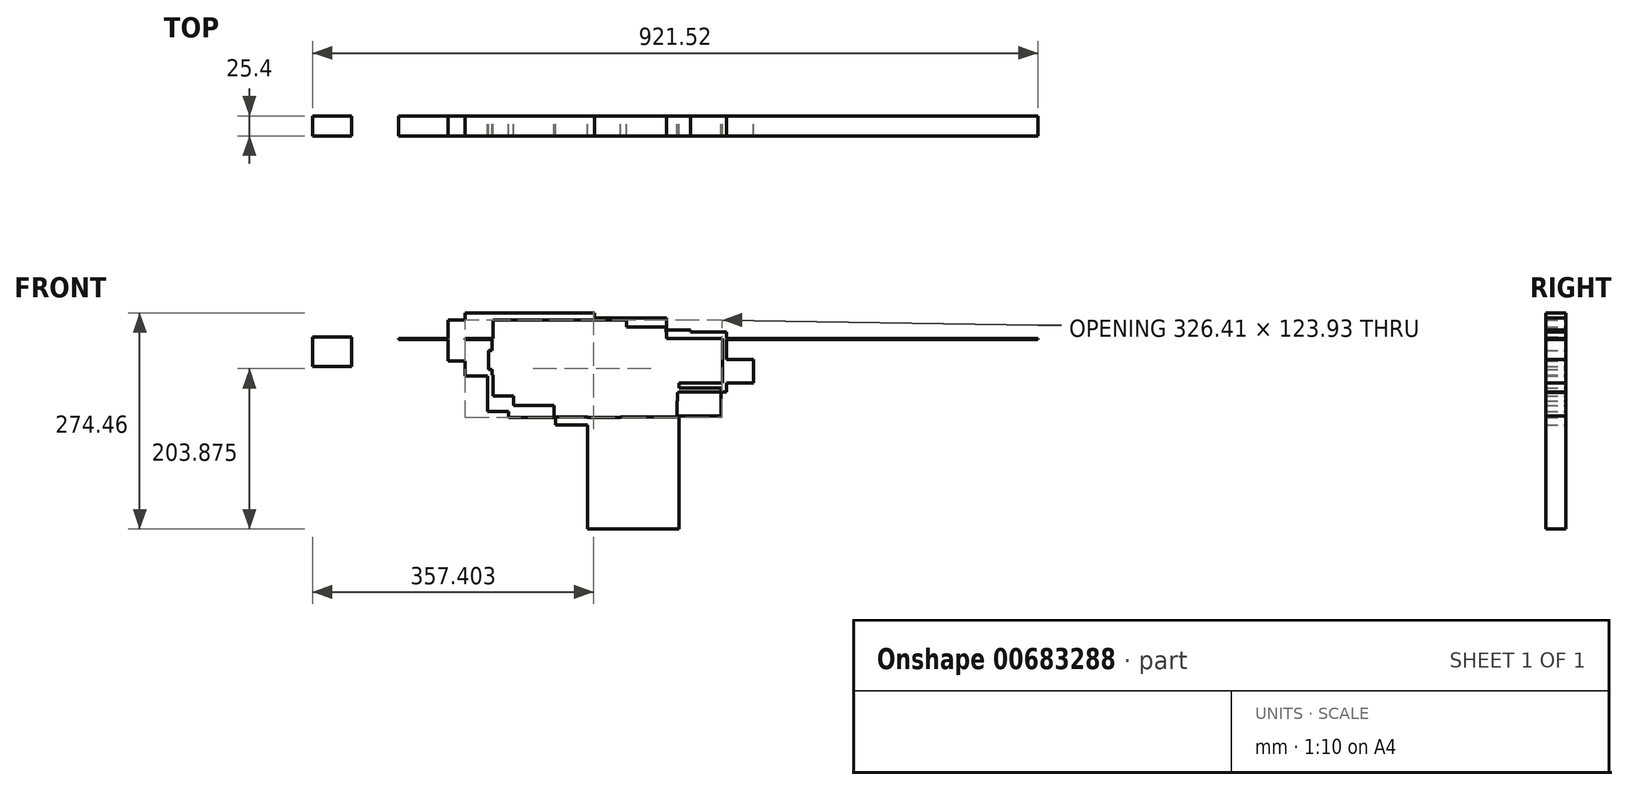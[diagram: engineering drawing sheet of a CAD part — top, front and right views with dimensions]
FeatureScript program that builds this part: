
annotation { "Feature Type Name" : "Feature", "Feature Type Description" : "" }
export const myFeature = defineFeature(function(context is Context, id is Id, definition is map)
    precondition{}
    {
        {
            var Q0;
            Q0=qCreatedBy(makeId("Front.planeOp"),FACE);
            var sketch = newSketch(context, id + "F0", { "sketchPlane" : qUnion([Q0])});
            skLineSegment(sketch, "E0.bottom", {"start": v(0, 0) * mm, "end": v(49.91, 0) * mm});
            skLineSegment(sketch, "E0.top", {"start": v(0, 37.47) * mm, "end": v(49.91, 37.47) * mm});
            skLineSegment(sketch, "E0.left", {"start": v(0, 0) * mm, "end": v(0, 37.47) * mm});
            skLineSegment(sketch, "E0.right", {"start": v(49.91, 0) * mm, "end": v(49.91, 37.47) * mm});
            skLineSegment(sketch, "E1.bottom", {"start": v(49.91, -36.2) * mm, "end": v(49.91, -36.2) * mm});
            skLineSegment(sketch, "E1.top", {"start": v(49.91, -12.83) * mm, "end": v(49.91, -12.83) * mm});
            skLineSegment(sketch, "E1.left", {"start": v(49.91, -36.2) * mm, "end": v(49.91, -12.83) * mm});
            skLineSegment(sketch, "E1.right", {"start": v(49.91, -36.2) * mm, "end": v(49.91, -12.83) * mm});
            skLineSegment(sketch, "E2.bottom", {"start": v(109.35, 35.43) * mm, "end": v(921.52, 35.43) * mm});
            skLineSegment(sketch, "E2.top", {"start": v(109.35, 34.42) * mm, "end": v(921.52, 34.42) * mm});
            skLineSegment(sketch, "E2.left", {"start": v(109.35, 35.43) * mm, "end": v(109.35, 34.42) * mm});
            skLineSegment(sketch, "E2.right", {"start": v(921.52, 35.43) * mm, "end": v(921.52, 34.42) * mm});
            skLineSegment(sketch, "E3.bottom", {"start": v(355.75, -9.52) * mm, "end": v(429.42, -9.52) * mm});
            skLineSegment(sketch, "E3.top", {"start": v(355.75, 31.07) * mm, "end": v(429.42, 31.07) * mm});
            skLineSegment(sketch, "E3.left", {"start": v(355.75, -9.52) * mm, "end": v(355.75, 31.07) * mm});
            skLineSegment(sketch, "E3.right", {"start": v(429.42, -9.52) * mm, "end": v(429.42, 31.07) * mm});
            skLineSegment(sketch, "E4.bottom", {"start": v(518.7, -27.12) * mm, "end": v(397.54, -27.12) * mm});
            skLineSegment(sketch, "E4.top", {"start": v(518.7, -63.04) * mm, "end": v(397.54, -63.04) * mm});
            skLineSegment(sketch, "E4.left", {"start": v(518.7, -27.12) * mm, "end": v(518.7, -63.04) * mm});
            skLineSegment(sketch, "E4.right", {"start": v(397.54, -27.12) * mm, "end": v(397.54, -63.04) * mm});
            skLineSegment(sketch, "E5.bottom", {"start": v(443.51, -56.93) * mm, "end": v(222.77, -56.93) * mm});
            skLineSegment(sketch, "E5.top", {"start": v(443.51, -4.85) * mm, "end": v(222.77, -4.85) * mm});
            skLineSegment(sketch, "E5.left", {"start": v(443.51, -56.93) * mm, "end": v(443.51, -4.85) * mm});
            skLineSegment(sketch, "E5.right", {"start": v(222.77, -56.93) * mm, "end": v(222.77, -4.85) * mm});
            skLineSegment(sketch, "E6.bottom", {"start": v(391.37, -64.48) * mm, "end": v(249.08, -64.48) * mm});
            skLineSegment(sketch, "E6.top", {"start": v(391.37, -7) * mm, "end": v(249.08, -7) * mm});
            skLineSegment(sketch, "E6.left", {"start": v(391.37, -64.48) * mm, "end": v(391.37, -7) * mm});
            skLineSegment(sketch, "E6.right", {"start": v(249.08, -64.48) * mm, "end": v(249.08, -7) * mm});
            skLineSegment(sketch, "E7.bottom", {"start": v(434.23, -49.4) * mm, "end": v(255.22, -49.4) * mm});
            skLineSegment(sketch, "E7.top", {"start": v(434.23, 18.86) * mm, "end": v(255.22, 18.86) * mm});
            skLineSegment(sketch, "E7.left", {"start": v(434.23, -49.4) * mm, "end": v(434.23, 18.86) * mm});
            skLineSegment(sketch, "E7.right", {"start": v(255.22, -49.4) * mm, "end": v(255.22, 18.86) * mm});
            skLineSegment(sketch, "E8.bottom", {"start": v(520.6, -32.87) * mm, "end": v(304.97, -32.87) * mm});
            skLineSegment(sketch, "E8.top", {"start": v(520.6, 44) * mm, "end": v(304.97, 44) * mm});
            skLineSegment(sketch, "E8.left", {"start": v(520.6, -32.87) * mm, "end": v(520.6, 44) * mm});
            skLineSegment(sketch, "E8.right", {"start": v(304.97, -32.87) * mm, "end": v(304.97, 44) * mm});
            skLineSegment(sketch, "E9.bottom", {"start": v(480.04, -0.9) * mm, "end": v(321.76, -0.9) * mm});
            skLineSegment(sketch, "E9.top", {"start": v(480.04, 46.16) * mm, "end": v(321.76, 46.16) * mm});
            skLineSegment(sketch, "E9.left", {"start": v(480.04, -0.9) * mm, "end": v(480.04, 46.16) * mm});
            skLineSegment(sketch, "E9.right", {"start": v(321.76, -0.9) * mm, "end": v(321.76, 46.16) * mm});
            skLineSegment(sketch, "E10.bottom", {"start": v(560.47, -20.65) * mm, "end": v(323.75, -20.65) * mm});
            skLineSegment(sketch, "E10.top", {"start": v(560.47, 8.8) * mm, "end": v(323.75, 8.8) * mm});
            skLineSegment(sketch, "E10.left", {"start": v(560.47, -20.65) * mm, "end": v(560.47, 8.8) * mm});
            skLineSegment(sketch, "E10.right", {"start": v(323.75, -20.65) * mm, "end": v(323.75, 8.8) * mm});
            skLineSegment(sketch, "E11.bottom", {"start": v(526.1, -32.5) * mm, "end": v(287.37, -32.5) * mm});
            skLineSegment(sketch, "E11.top", {"start": v(526.1, 44) * mm, "end": v(287.37, 44) * mm});
            skLineSegment(sketch, "E11.left", {"start": v(526.1, -32.5) * mm, "end": v(526.1, 44) * mm});
            skLineSegment(sketch, "E11.right", {"start": v(287.37, -32.5) * mm, "end": v(287.37, 44) * mm});
            skLineSegment(sketch, "E12.bottom", {"start": v(378.2, -5.2) * mm, "end": v(240.43, -5.2) * mm});
            skLineSegment(sketch, "E12.top", {"start": v(378.2, 32.15) * mm, "end": v(240.43, 32.15) * mm});
            skLineSegment(sketch, "E12.left", {"start": v(378.2, -5.2) * mm, "end": v(378.2, 32.15) * mm});
            skLineSegment(sketch, "E12.right", {"start": v(240.43, -5.2) * mm, "end": v(240.43, 32.15) * mm});
            skLineSegment(sketch, "E13.bottom", {"start": v(449.66, -37.18) * mm, "end": v(229.4, -37.18) * mm});
            skLineSegment(sketch, "E13.top", {"start": v(449.66, 61.96) * mm, "end": v(229.4, 61.96) * mm});
            skLineSegment(sketch, "E13.left", {"start": v(449.66, -37.18) * mm, "end": v(449.66, 61.96) * mm});
            skLineSegment(sketch, "E13.right", {"start": v(229.4, -37.18) * mm, "end": v(229.4, 61.96) * mm});
            skLineSegment(sketch, "E14.bottom", {"start": v(388.16, 3.05) * mm, "end": v(269.8, 3.05) * mm});
            skLineSegment(sketch, "E14.top", {"start": v(388.16, 28.2) * mm, "end": v(269.8, 28.2) * mm});
            skLineSegment(sketch, "E14.left", {"start": v(388.16, 3.05) * mm, "end": v(388.16, 28.2) * mm});
            skLineSegment(sketch, "E14.right", {"start": v(269.8, 3.05) * mm, "end": v(269.8, 28.2) * mm});
            skLineSegment(sketch, "E15.bottom", {"start": v(448.95, -7.72) * mm, "end": v(294.65, -7.72) * mm});
            skLineSegment(sketch, "E15.top", {"start": v(448.95, 50.47) * mm, "end": v(294.65, 50.47) * mm});
            skLineSegment(sketch, "E15.left", {"start": v(448.95, -7.72) * mm, "end": v(448.95, 50.47) * mm});
            skLineSegment(sketch, "E15.right", {"start": v(294.65, -7.72) * mm, "end": v(294.65, 50.47) * mm});
            skLineSegment(sketch, "E16.bottom", {"start": v(384.93, 23.89) * mm, "end": v(234.65, 23.89) * mm});
            skLineSegment(sketch, "E16.top", {"start": v(384.93, 41.85) * mm, "end": v(234.65, 41.85) * mm});
            skLineSegment(sketch, "E16.left", {"start": v(384.93, 23.89) * mm, "end": v(384.93, 41.85) * mm});
            skLineSegment(sketch, "E16.right", {"start": v(234.65, 23.89) * mm, "end": v(234.65, 41.85) * mm});
            skLineSegment(sketch, "E17.bottom", {"start": v(377.93, 7.36) * mm, "end": v(172.27, 7.36) * mm});
            skLineSegment(sketch, "E17.top", {"start": v(377.93, 59.45) * mm, "end": v(172.27, 59.45) * mm});
            skLineSegment(sketch, "E17.left", {"start": v(377.93, 7.36) * mm, "end": v(377.93, 59.45) * mm});
            skLineSegment(sketch, "E17.right", {"start": v(172.27, 7.36) * mm, "end": v(172.27, 59.45) * mm});
            skLineSegment(sketch, "E18.bottom", {"start": v(352, 12.03) * mm, "end": v(271.51, 12.03) * mm});
            skLineSegment(sketch, "E18.top", {"start": v(352, 30.35) * mm, "end": v(271.51, 30.35) * mm});
            skLineSegment(sketch, "E18.left", {"start": v(352, 12.03) * mm, "end": v(352, 30.35) * mm});
            skLineSegment(sketch, "E18.right", {"start": v(271.51, 12.03) * mm, "end": v(271.51, 30.35) * mm});
            skLineSegment(sketch, "E19.bottom", {"start": v(426.15, -24.25) * mm, "end": v(309.92, -24.25) * mm});
            skLineSegment(sketch, "E19.top", {"start": v(426.15, 4.5) * mm, "end": v(309.92, 4.5) * mm});
            skLineSegment(sketch, "E19.left", {"start": v(426.15, -24.25) * mm, "end": v(426.15, 4.5) * mm});
            skLineSegment(sketch, "E19.right", {"start": v(309.92, -24.25) * mm, "end": v(309.92, 4.5) * mm});
            skLineSegment(sketch, "E20.bottom", {"start": v(403.97, -32.5) * mm, "end": v(278.23, -32.5) * mm});
            skLineSegment(sketch, "E20.top", {"start": v(403.97, 15.27) * mm, "end": v(278.23, 15.27) * mm});
            skLineSegment(sketch, "E20.left", {"start": v(403.97, -32.5) * mm, "end": v(403.97, 15.27) * mm});
            skLineSegment(sketch, "E20.right", {"start": v(278.23, -32.5) * mm, "end": v(278.23, 15.27) * mm});
            skLineSegment(sketch, "E21.bottom", {"start": v(331.57, -3.77) * mm, "end": v(223.41, -3.77) * mm});
            skLineSegment(sketch, "E21.top", {"start": v(331.57, 20.65) * mm, "end": v(223.41, 20.65) * mm});
            skLineSegment(sketch, "E21.left", {"start": v(331.57, -3.77) * mm, "end": v(331.57, 20.65) * mm});
            skLineSegment(sketch, "E21.right", {"start": v(223.41, -3.77) * mm, "end": v(223.41, 20.65) * mm});
            skLineSegment(sketch, "E22.bottom", {"start": v(462.96, -64.12) * mm, "end": v(306.63, -64.12) * mm});
            skLineSegment(sketch, "E22.top", {"start": v(462.96, -17.78) * mm, "end": v(306.63, -17.78) * mm});
            skLineSegment(sketch, "E22.left", {"start": v(462.96, -64.12) * mm, "end": v(462.96, -17.78) * mm});
            skLineSegment(sketch, "E22.right", {"start": v(306.63, -64.12) * mm, "end": v(306.63, -17.78) * mm});
            skLineSegment(sketch, "E23.bottom", {"start": v(443.13, -74.18) * mm, "end": v(308.98, -74.18) * mm});
            skLineSegment(sketch, "E23.top", {"start": v(443.13, -4.85) * mm, "end": v(308.98, -4.85) * mm});
            skLineSegment(sketch, "E23.left", {"start": v(443.13, -74.18) * mm, "end": v(443.13, -4.85) * mm});
            skLineSegment(sketch, "E23.right", {"start": v(308.98, -74.18) * mm, "end": v(308.98, -4.85) * mm});
            skLineSegment(sketch, "E24.bottom", {"start": v(463.57, -43.64) * mm, "end": v(283.86, -43.64) * mm});
            skLineSegment(sketch, "E24.top", {"start": v(463.57, 12.4) * mm, "end": v(283.86, 12.4) * mm});
            skLineSegment(sketch, "E24.left", {"start": v(463.57, -43.64) * mm, "end": v(463.57, 12.4) * mm});
            skLineSegment(sketch, "E24.right", {"start": v(283.86, -43.64) * mm, "end": v(283.86, 12.4) * mm});
            skLineSegment(sketch, "E25.bottom", {"start": v(358.6, -12.03) * mm, "end": v(194.2, -12.03) * mm});
            skLineSegment(sketch, "E25.top", {"start": v(358.6, 68.07) * mm, "end": v(194.2, 68.07) * mm});
            skLineSegment(sketch, "E25.left", {"start": v(358.6, -12.03) * mm, "end": v(358.6, 68.07) * mm});
            skLineSegment(sketch, "E25.right", {"start": v(194.2, -12.03) * mm, "end": v(194.2, 68.07) * mm});
            skLineSegment(sketch, "E26.bottom", {"start": v(395.66, -10.6) * mm, "end": v(227.98, -10.6) * mm});
            skLineSegment(sketch, "E26.top", {"start": v(395.66, 35.02) * mm, "end": v(227.98, 35.02) * mm});
            skLineSegment(sketch, "E26.left", {"start": v(395.66, -10.6) * mm, "end": v(395.66, 35.02) * mm});
            skLineSegment(sketch, "E26.right", {"start": v(227.98, -10.6) * mm, "end": v(227.98, 35.02) * mm});
            skLineSegment(sketch, "E27.bottom", {"start": v(398.83, -12.03) * mm, "end": v(231.9, -12.03) * mm});
            skLineSegment(sketch, "E27.top", {"start": v(398.83, 59.45) * mm, "end": v(231.9, 59.45) * mm});
            skLineSegment(sketch, "E27.left", {"start": v(398.83, -12.03) * mm, "end": v(398.83, 59.45) * mm});
            skLineSegment(sketch, "E27.right", {"start": v(231.9, -12.03) * mm, "end": v(231.9, 59.45) * mm});
            skLineSegment(sketch, "E28.bottom", {"start": v(465.93, -1.26) * mm, "end": v(349.4, -1.26) * mm});
            skLineSegment(sketch, "E28.top", {"start": v(465.93, -206.39) * mm, "end": v(349.4, -206.39) * mm});
            skLineSegment(sketch, "E28.left", {"start": v(465.93, -1.26) * mm, "end": v(465.93, -206.39) * mm});
            skLineSegment(sketch, "E28.right", {"start": v(349.4, -1.26) * mm, "end": v(349.4, -206.39) * mm});
            skSolve(sketch);
        }
        {
            var Q0;
            Q0 = qSketchRegion(id + "F0", true);
            extrude(context, id + "F1", {"entities" : qUnion([Q0]), "depth" : 25.4 * mm, "offsetDistance" : 25.4 * mm});
        }
    });
